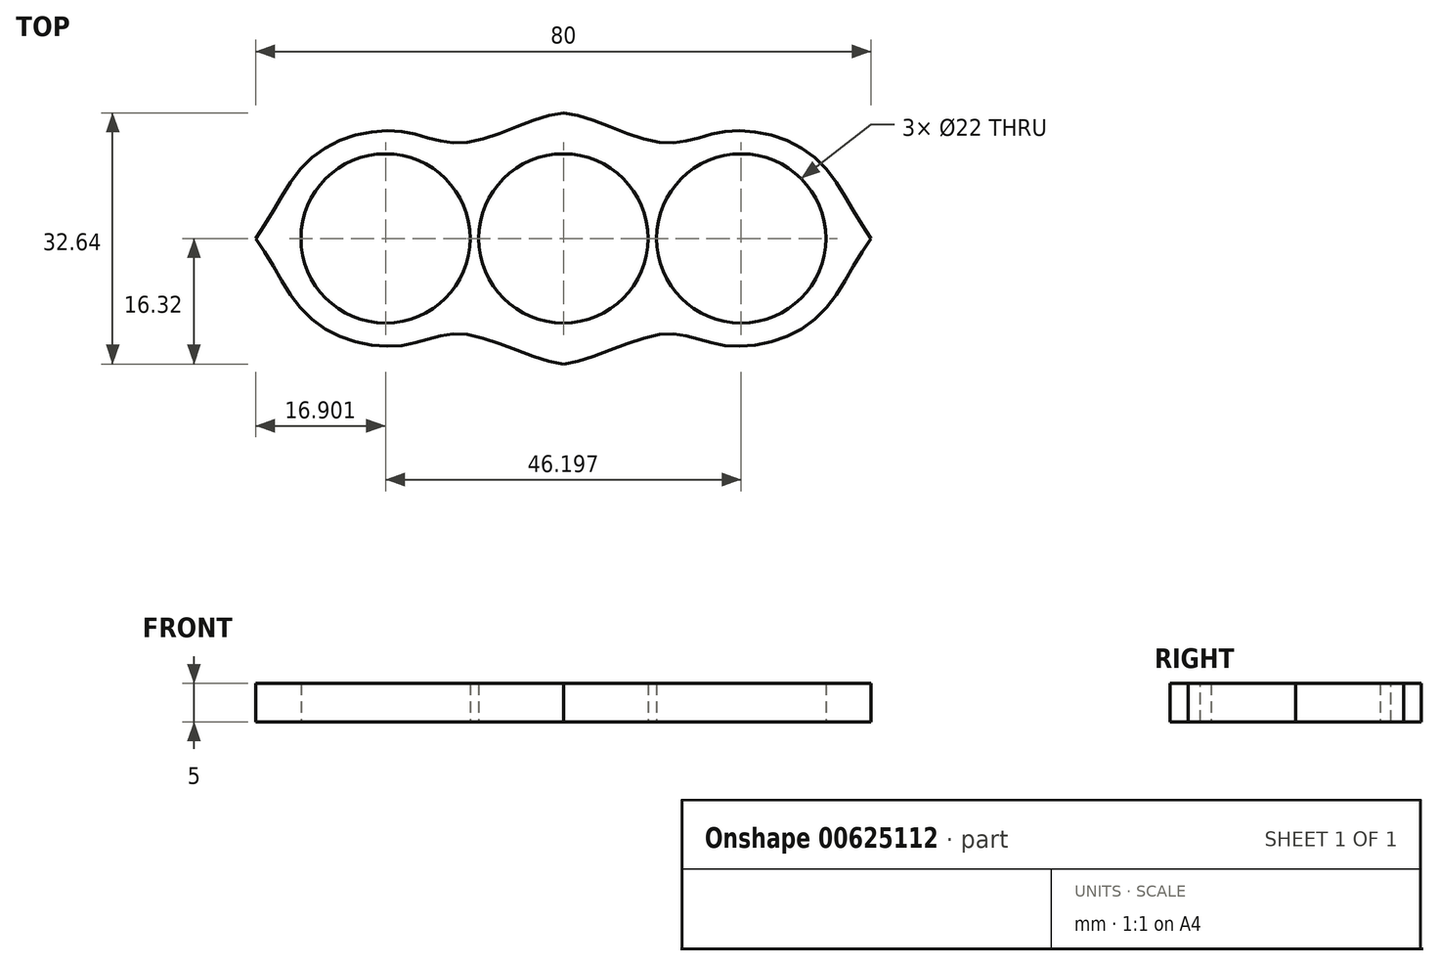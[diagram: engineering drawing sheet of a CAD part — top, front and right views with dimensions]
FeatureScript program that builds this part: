
annotation { "Feature Type Name" : "Feature", "Feature Type Description" : "" }
export const myFeature = defineFeature(function(context is Context, id is Id, definition is map)
    precondition{}
    {
        {
            var Q0;
            Q0=qCreatedBy(makeId("Top.planeOp"),FACE);
            var sketch = newSketch(context, id + "F0", { "sketchPlane" : qUnion([Q0])});
            skFitSpline(sketch, "E0", {"points": [v(0, 16.32) * mm, v(-12.8, 12.44) * mm, v(-21.2, 13.92) * mm, v(-32.57, 10.6) * mm, v(-40, 0) * mm], "startDerivative": vector(-39.82, -3.09) * mm, "endDerivative": vector(-28.97, -38.45) * mm});
            skFitSpline(sketch, "E1.MirrorCS", {"points": [v(0, 16.32) * mm, v(12.8, 12.44) * mm, v(21.2, 13.92) * mm, v(32.57, 10.6) * mm, v(40, 0) * mm], "startDerivative": vector(39.82, -3.09) * mm, "endDerivative": vector(28.97, -38.45) * mm});
            skFitSpline(sketch, "E2.MirrorCS", {"points": [v(0, -16.32) * mm, v(-12.8, -12.44) * mm, v(-21.2, -13.92) * mm, v(-32.57, -10.6) * mm, v(-40, 0) * mm], "startDerivative": vector(-39.82, 3.09) * mm, "endDerivative": vector(-28.97, 38.45) * mm});
            skFitSpline(sketch, "E3.MirrorCS", {"points": [v(0, -16.32) * mm, v(12.8, -12.44) * mm, v(21.2, -13.92) * mm, v(32.57, -10.6) * mm, v(40, 0) * mm], "startDerivative": vector(39.82, 3.09) * mm, "endDerivative": vector(28.97, 38.45) * mm});
            skSolve(sketch);
        }
        {
            var Q0;
            Q0=qCreatedBy(makeId("Top.planeOp"),FACE);
            var sketch = newSketch(context, id + "F1", { "sketchPlane" : qUnion([Q0])});
            skCircle(sketch, "E4", {"center": v(0, 0) * mm, "radius": 11 * mm});
            skCircle(sketch, "E5", {"center": v(-23.1, 0) * mm, "radius": 11 * mm});
            skCircle(sketch, "E6.MirrorC", {"center": v(23.1, 0) * mm, "radius": 11 * mm});
            skSolve(sketch);
        }
        {
            var Q0;
            Q0=makeQuery(id+"F0.imprint","IMPRINT",FACE,{"disambiguationData":[TD([[makeQuery(id+"F0.imprint","IMPRINT",EDGE,{"derivedFrom":sQuery(id+"F0.wireOp",EDGE,"E0")}),1.0]])]});
            extrude(context, id + "F2", {"entities" : qUnion([Q0]), "depth" : 5 * mm, "offsetDistance" : 25 * mm});
        }
        {
            var Q0;
            Q0 = qSketchRegion(id + "F1", true);
            extrude(context, id + "F3", {"entities" : qUnion([Q0]), "operationType" : NewBodyOperationType.REMOVE, "depth" : 25 * mm, "offsetDistance" : 25 * mm});
        }
    });
